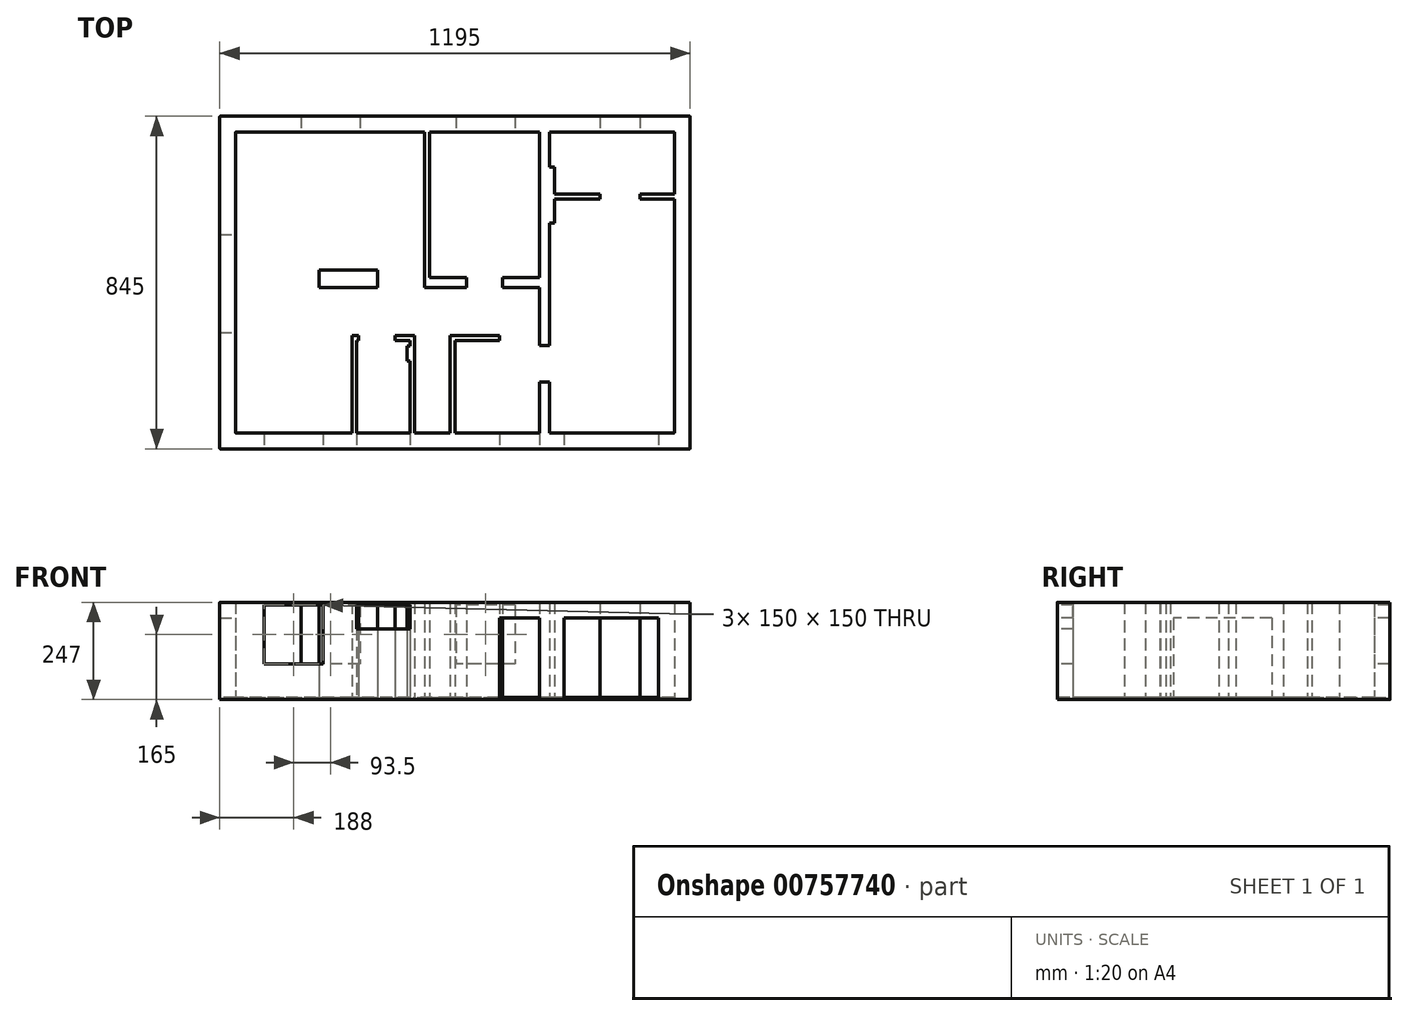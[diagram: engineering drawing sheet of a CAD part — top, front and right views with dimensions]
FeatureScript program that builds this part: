
annotation { "Feature Type Name" : "Feature", "Feature Type Description" : "" }
export const myFeature = defineFeature(function(context is Context, id is Id, definition is map)
    precondition{}
    {
        {
            var Q0;
            Q0=qCreatedBy(makeId("Top.planeOp"),FACE);
            var sketch = newSketch(context, id + "F0", { "sketchPlane" : qUnion([Q0])});
            skLineSegment(sketch, "E0", {"start": v(0, 0) * mm, "end": v(1145, 0) * mm, "construction": true});
            skLineSegment(sketch, "E1", {"start": v(1145, 0) * mm, "end": v(1145, 795) * mm, "construction": true});
            skLineSegment(sketch, "E2", {"start": v(1145, 795) * mm, "end": v(0, 795) * mm, "construction": true});
            skLineSegment(sketch, "E3", {"start": v(0, 795) * mm, "end": v(0, 0) * mm, "construction": true});
            skLineSegment(sketch, "E4", {"start": v(800, 0) * mm, "end": v(800, 795) * mm, "construction": true});
            skLineSegment(sketch, "E5", {"start": v(800, 397.5) * mm, "end": v(0, 397.5) * mm, "construction": true});
            skLineSegment(sketch, "E6.0", {"start": v(1170, 820) * mm, "end": v(-25, 820) * mm});
            skLineSegment(sketch, "E6.1", {"start": v(1170, -25) * mm, "end": v(1170, 820) * mm});
            skLineSegment(sketch, "E6.2", {"start": v(-25, -25) * mm, "end": v(1170, -25) * mm});
            skLineSegment(sketch, "E6.3", {"start": v(-25, 820) * mm, "end": v(-25, -25) * mm});
            skLineSegment(sketch, "E7.0", {"start": v(1130, 780) * mm, "end": v(15, 780) * mm});
            skLineSegment(sketch, "E7.1", {"start": v(1130, 15) * mm, "end": v(1130, 780) * mm});
            skLineSegment(sketch, "E7.2", {"start": v(15, 15) * mm, "end": v(1130, 15) * mm});
            skLineSegment(sketch, "E7.3", {"start": v(15, 780) * mm, "end": v(15, 15) * mm});
            skLineSegment(sketch, "E8.0", {"start": v(812.5, 0) * mm, "end": v(812.5, 795) * mm});
            skLineSegment(sketch, "E9.0", {"start": v(800, 410) * mm, "end": v(0, 410) * mm});
            skLineSegment(sketch, "E10.0", {"start": v(800, 385) * mm, "end": v(0, 385) * mm});
            skLineSegment(sketch, "E11.0", {"start": v(787.5, 0) * mm, "end": v(787.5, 795) * mm});
            skLineSegment(sketch, "E12", {"start": v(1090, 15) * mm, "end": v(1090, -25) * mm});
            skLineSegment(sketch, "E13", {"start": v(850, 15) * mm, "end": v(850, -25) * mm});
            skLineSegment(sketch, "E14", {"start": v(787.5, 15) * mm, "end": v(787.5, -25) * mm});
            skLineSegment(sketch, "E15", {"start": v(685.5, 15) * mm, "end": v(685.5, -25) * mm});
            skLineSegment(sketch, "E16", {"start": v(572.5, 15) * mm, "end": v(572.5, 250.5) * mm});
            skLineSegment(sketch, "E17", {"start": v(572.5, 250.5) * mm, "end": v(685.5, 250.5) * mm});
            skLineSegment(sketch, "E18.0", {"start": v(560.5, 262.5) * mm, "end": v(685.5, 262.5) * mm});
            skLineSegment(sketch, "E18.1", {"start": v(560.5, 15) * mm, "end": v(560.5, 262.5) * mm});
            skLineSegment(sketch, "E19", {"start": v(685.5, 262.5) * mm, "end": v(685.5, 250.5) * mm});
            skLineSegment(sketch, "E20", {"start": v(470.5, 15) * mm, "end": v(470.5, 262.5) * mm});
            skLineSegment(sketch, "E21", {"start": v(470.5, 262.5) * mm, "end": v(420, 262.5) * mm});
            skLineSegment(sketch, "E22", {"start": v(420, 262.5) * mm, "end": v(420, 250.5) * mm});
            skLineSegment(sketch, "E23", {"start": v(420, 250.5) * mm, "end": v(458.5, 250.5) * mm});
            skLineSegment(sketch, "E24", {"start": v(458.5, 250.5) * mm, "end": v(458.5, 236.22) * mm});
            skLineSegment(sketch, "E25", {"start": v(458.5, 236.22) * mm, "end": v(450.5, 236.22) * mm});
            skLineSegment(sketch, "E26", {"start": v(450.5, 236.22) * mm, "end": v(450.5, 198.5) * mm});
            skLineSegment(sketch, "E27", {"start": v(450.5, 198.5) * mm, "end": v(458.5, 198.5) * mm});
            skLineSegment(sketch, "E28", {"start": v(458.5, 198.5) * mm, "end": v(458.5, 15) * mm});
            skLineSegment(sketch, "E29", {"start": v(787.5, 145) * mm, "end": v(812.5, 145) * mm});
            skLineSegment(sketch, "E30", {"start": v(787.5, 237) * mm, "end": v(812.5, 237) * mm});
            skLineSegment(sketch, "E31", {"start": v(693.5, 410) * mm, "end": v(693.5, 385) * mm});
            skLineSegment(sketch, "E32", {"start": v(601.5, 410) * mm, "end": v(601.5, 385) * mm});
            skLineSegment(sketch, "E33", {"start": v(507.5, 780) * mm, "end": v(507.5, 410) * mm});
            skLineSegment(sketch, "E34", {"start": v(495.5, 780) * mm, "end": v(495.5, 410) * mm});
            skLineSegment(sketch, "E35", {"start": v(495.5, 410) * mm, "end": v(495.5, 385) * mm});
            skLineSegment(sketch, "E36", {"start": v(812.5, 691) * mm, "end": v(825.5, 691) * mm});
            skLineSegment(sketch, "E37", {"start": v(825.5, 691) * mm, "end": v(825.5, 549) * mm});
            skLineSegment(sketch, "E38", {"start": v(825.5, 549) * mm, "end": v(812.5, 549) * mm});
            skLineSegment(sketch, "E39", {"start": v(825.5, 622) * mm, "end": v(1130, 622) * mm});
            skLineSegment(sketch, "E40", {"start": v(825.5, 610) * mm, "end": v(1130, 610) * mm});
            skLineSegment(sketch, "E41", {"start": v(940.5, 622) * mm, "end": v(940.5, 610) * mm});
            skLineSegment(sketch, "E42", {"start": v(1042.5, 622) * mm, "end": v(1042.5, 610) * mm});
            skLineSegment(sketch, "E43", {"start": v(940.5, 820) * mm, "end": v(940.5, 780) * mm});
            skLineSegment(sketch, "E44", {"start": v(1042.5, 820) * mm, "end": v(1042.5, 780) * mm});
            skLineSegment(sketch, "E45", {"start": v(375.5, 385) * mm, "end": v(375.5, 429) * mm});
            skLineSegment(sketch, "E46", {"start": v(375.5, 429) * mm, "end": v(227.5, 429) * mm});
            skLineSegment(sketch, "E47", {"start": v(227.5, 429) * mm, "end": v(227.5, 385) * mm});
            skLineSegment(sketch, "E48", {"start": v(-25, 520) * mm, "end": v(15, 520) * mm});
            skLineSegment(sketch, "E49", {"start": v(-25, 270) * mm, "end": v(15, 270) * mm});
            skLineSegment(sketch, "E50", {"start": v(311, 15) * mm, "end": v(311, 262.5) * mm});
            skLineSegment(sketch, "E51", {"start": v(311, 262.5) * mm, "end": v(328, 262.5) * mm});
            skLineSegment(sketch, "E52", {"start": v(328, 262.5) * mm, "end": v(328, 250.5) * mm});
            skLineSegment(sketch, "E53", {"start": v(328, 250.5) * mm, "end": v(323, 250.5) * mm});
            skLineSegment(sketch, "E54", {"start": v(323, 250.5) * mm, "end": v(323, 15) * mm});
            skLineSegment(sketch, "E55", {"start": v(181.5, 820) * mm, "end": v(181.5, 780) * mm});
            skLineSegment(sketch, "E56", {"start": v(331.5, 820) * mm, "end": v(331.5, 780) * mm});
            skLineSegment(sketch, "E57", {"start": v(575, 820) * mm, "end": v(575, 780) * mm});
            skLineSegment(sketch, "E58", {"start": v(725, 820) * mm, "end": v(725, 780) * mm});
            skLineSegment(sketch, "E59", {"start": v(88, 15) * mm, "end": v(88, -25) * mm});
            skLineSegment(sketch, "E60", {"start": v(238, 15) * mm, "end": v(238, -25) * mm});
            skLineSegment(sketch, "E61", {"start": v(323, 15) * mm, "end": v(323, -25) * mm});
            skLineSegment(sketch, "E62", {"start": v(458.5, 15) * mm, "end": v(458.5, -25) * mm});
            skSolve(sketch);
        }
        {
            var Q0;
            {var subQ5=sQuery(id+"F0.wireOp",EDGE,"E6.1");Q0=makeQuery(id+"F0.imprint","IMPRINT",FACE,{"disambiguationData":[TD([[makeQuery(id+"F0.imprint","IMPRINT",EDGE,{"derivedFrom":subQ5}),1.0]])]});}
            var Q1;
            {var subQ0=sQuery(id+"F0.wireOp",EDGE,"E43");Q1=makeQuery(id+"F0.imprint","IMPRINT",FACE,{"disambiguationData":[TD([[makeQuery(id+"F0.imprint","IMPRINT",EDGE,{"derivedFrom":subQ0}),1.0]])]});}
            var Q2;
            {var subQ4=sQuery(id+"F0.wireOp",EDGE,"E43");Q2=makeQuery(id+"F0.imprint","IMPRINT",FACE,{"disambiguationData":[TD([[makeQuery(id+"F0.imprint","IMPRINT",EDGE,{"derivedFrom":subQ4}),-1.0]])]});}
            var Q3;
            {var subQ5=sQuery(id+"F0.wireOp",EDGE,"E48");Q3=makeQuery(id+"F0.imprint","IMPRINT",FACE,{"disambiguationData":[TD([[makeQuery(id+"F0.imprint","IMPRINT",EDGE,{"derivedFrom":subQ5}),-1.0]])]});}
            var Q4;
            {var subQ3=sQuery(id+"F0.wireOp",EDGE,"E15");Q4=makeQuery(id+"F0.imprint","IMPRINT",FACE,{"disambiguationData":[TD([[makeQuery(id+"F0.imprint","IMPRINT",EDGE,{"derivedFrom":subQ3}),-1.0]])]});}
            var Q5;
            {var subQ0=sQuery(id+"F0.wireOp",EDGE,"E14");Q5=makeQuery(id+"F0.imprint","IMPRINT",FACE,{"disambiguationData":[TD([[makeQuery(id+"F0.imprint","IMPRINT",EDGE,{"derivedFrom":subQ0}),-1.0]])]});}
            var Q6;
            {var subQ4=sQuery(id+"F0.wireOp",EDGE,"E13");Q6=makeQuery(id+"F0.imprint","IMPRINT",FACE,{"disambiguationData":[TD([[makeQuery(id+"F0.imprint","IMPRINT",EDGE,{"derivedFrom":subQ4}),-1.0]])]});}
            var Q7;
            {var subQ2=sQuery(id+"F0.wireOp",EDGE,"E12");Q7=makeQuery(id+"F0.imprint","IMPRINT",FACE,{"disambiguationData":[TD([[makeQuery(id+"F0.imprint","IMPRINT",EDGE,{"derivedFrom":subQ2}),-1.0]])]});}
            var Q8;
            {var subQ0=sQuery(id+"F0.wireOp",EDGE,"E38");Q8=makeQuery(id+"F0.imprint","IMPRINT",FACE,{"disambiguationData":[TD([[makeQuery(id+"F0.imprint","IMPRINT",EDGE,{"derivedFrom":subQ0}),1.0]])]});}
            var Q9;
            {var subQ3=sQuery(id+"F0.wireOp",EDGE,"E31");Q9=makeQuery(id+"F0.imprint","IMPRINT",FACE,{"disambiguationData":[TD([[makeQuery(id+"F0.imprint","IMPRINT",EDGE,{"derivedFrom":subQ3}),1.0]])]});}
            var Q10;
            {var subQ0=sQuery(id+"F0.wireOp",EDGE,"E47");var subQ1=sQuery(id+"F0.wireOp",EDGE,"E9.0");var subQ2=makeQuery(id+"F0.imprint","INTERSECT",VERTEX,{"derivedFrom":[subQ1,subQ0]});Q10=makeQuery(id+"F0.imprint","IMPRINT",FACE,{"disambiguationData":[TD([[makeQuery(id+"F0.imprint","IMPRINT",EDGE,{"disambiguationData":[TD([[subQ2,1.0]])],"derivedFrom":subQ1}),1.0]])]});}
            var Q11;
            {var subQ0=sQuery(id+"F0.wireOp",EDGE,"E31");Q11=makeQuery(id+"F0.imprint","IMPRINT",FACE,{"disambiguationData":[TD([[makeQuery(id+"F0.imprint","IMPRINT",EDGE,{"derivedFrom":subQ0}),-1.0]])]});}
            var Q12;
            {var subQ0=sQuery(id+"F0.wireOp",EDGE,"E32");Q12=makeQuery(id+"F0.imprint","IMPRINT",FACE,{"disambiguationData":[TD([[makeQuery(id+"F0.imprint","IMPRINT",EDGE,{"derivedFrom":subQ0}),-1.0]])]});}
            var Q13;
            {var subQ0=sQuery(id+"F0.wireOp",EDGE,"E35");Q13=makeQuery(id+"F0.imprint","IMPRINT",FACE,{"disambiguationData":[TD([[makeQuery(id+"F0.imprint","IMPRINT",EDGE,{"derivedFrom":subQ0}),-1.0]])]});}
            var Q14;
            {var subQ1=sQuery(id+"F0.wireOp",EDGE,"E36");Q14=makeQuery(id+"F0.imprint","IMPRINT",FACE,{"disambiguationData":[TD([[makeQuery(id+"F0.imprint","IMPRINT",EDGE,{"derivedFrom":subQ1}),-1.0]])]});}
            var Q15;
            {var subQ5=sQuery(id+"F0.wireOp",EDGE,"E46");Q15=makeQuery(id+"F0.imprint","IMPRINT",FACE,{"disambiguationData":[TD([[makeQuery(id+"F0.imprint","IMPRINT",EDGE,{"derivedFrom":subQ5}),1.0]])]});}
            var Q16;
            {var subQ4=sQuery(id+"F0.wireOp",EDGE,"E34");Q16=makeQuery(id+"F0.imprint","IMPRINT",FACE,{"disambiguationData":[TD([[makeQuery(id+"F0.imprint","IMPRINT",EDGE,{"derivedFrom":subQ4}),-1.0]])]});}
            var Q17;
            {var subQ8=sQuery(id+"F0.wireOp",EDGE,"E36");Q17=makeQuery(id+"F0.imprint","IMPRINT",FACE,{"disambiguationData":[TD([[makeQuery(id+"F0.imprint","IMPRINT",EDGE,{"derivedFrom":subQ8}),1.0]])]});}
            var Q18;
            {var subQ0=sQuery(id+"F0.wireOp",EDGE,"E50");Q18=makeQuery(id+"F0.imprint","IMPRINT",FACE,{"disambiguationData":[TD([[makeQuery(id+"F0.imprint","IMPRINT",EDGE,{"derivedFrom":subQ0}),-1.0]])]});}
            var Q19;
            {var subQ13=sQuery(id+"F0.wireOp",EDGE,"E16");Q19=makeQuery(id+"F0.imprint","IMPRINT",FACE,{"disambiguationData":[TD([[makeQuery(id+"F0.imprint","IMPRINT",EDGE,{"derivedFrom":subQ13}),-1.0]])]});}
            var Q20;
            {var subQ4=sQuery(id+"F0.wireOp",EDGE,"E30");Q20=makeQuery(id+"F0.imprint","IMPRINT",FACE,{"disambiguationData":[TD([[makeQuery(id+"F0.imprint","IMPRINT",EDGE,{"derivedFrom":subQ4}),1.0]])]});}
            var Q21;
            {var subQ2=sQuery(id+"F0.wireOp",EDGE,"E29");Q21=makeQuery(id+"F0.imprint","IMPRINT",FACE,{"disambiguationData":[TD([[makeQuery(id+"F0.imprint","IMPRINT",EDGE,{"derivedFrom":subQ2}),1.0]])]});}
            var Q22;
            {var subQ0=sQuery(id+"F0.wireOp",EDGE,"E41");Q22=makeQuery(id+"F0.imprint","IMPRINT",FACE,{"disambiguationData":[TD([[makeQuery(id+"F0.imprint","IMPRINT",EDGE,{"derivedFrom":subQ0}),1.0]])]});}
            var Q23;
            {var subQ0=sQuery(id+"F0.wireOp",EDGE,"E16");Q23=makeQuery(id+"F0.imprint","IMPRINT",FACE,{"disambiguationData":[TD([[makeQuery(id+"F0.imprint","IMPRINT",EDGE,{"derivedFrom":subQ0}),1.0]])]});}
            var Q24;
            {var subQ2=sQuery(id+"F0.wireOp",EDGE,"E33");Q24=makeQuery(id+"F0.imprint","IMPRINT",FACE,{"disambiguationData":[TD([[makeQuery(id+"F0.imprint","IMPRINT",EDGE,{"derivedFrom":subQ2}),-1.0]])]});}
            var Q25;
            {var subQ5=sQuery(id+"F0.wireOp",EDGE,"E42");Q25=makeQuery(id+"F0.imprint","IMPRINT",FACE,{"disambiguationData":[TD([[makeQuery(id+"F0.imprint","IMPRINT",EDGE,{"derivedFrom":subQ5}),1.0]])]});}
            var Q26;
            {var subQ5=sQuery(id+"F0.wireOp",EDGE,"E29");Q26=makeQuery(id+"F0.imprint","IMPRINT",FACE,{"disambiguationData":[TD([[makeQuery(id+"F0.imprint","IMPRINT",EDGE,{"derivedFrom":subQ5}),-1.0]])]});}
            var Q27;
            {var subQ0=sQuery(id+"F0.wireOp",EDGE,"E10.0");var subQ1=sQuery(id+"F0.wireOp",EDGE,"E7.3");var subQ2=makeQuery(id+"F0.imprint","INTERSECT",VERTEX,{"derivedFrom":[subQ1,subQ0]});Q27=makeQuery(id+"F0.imprint","IMPRINT",FACE,{"disambiguationData":[TD([[makeQuery(id+"F0.imprint","IMPRINT",EDGE,{"disambiguationData":[TD([[subQ2,1.0]])],"derivedFrom":subQ1}),1.0]])]});}
            var Q28;
            {var subQ0=sQuery(id+"F0.wireOp",EDGE,"E20");Q28=makeQuery(id+"F0.imprint","IMPRINT",FACE,{"disambiguationData":[TD([[makeQuery(id+"F0.imprint","IMPRINT",EDGE,{"derivedFrom":subQ0}),1.0]])]});}
            var Q29;
            {var subQ5=sQuery(id+"F0.wireOp",EDGE,"E41");Q29=makeQuery(id+"F0.imprint","IMPRINT",FACE,{"disambiguationData":[TD([[makeQuery(id+"F0.imprint","IMPRINT",EDGE,{"derivedFrom":subQ5}),-1.0]])]});}
            var Q30;
            {var subQ2=sQuery(id+"F0.wireOp",EDGE,"E33");Q30=makeQuery(id+"F0.imprint","IMPRINT",FACE,{"disambiguationData":[TD([[makeQuery(id+"F0.imprint","IMPRINT",EDGE,{"derivedFrom":subQ2}),1.0]])]});}
            var Q31;
            {var subQ3=sQuery(id+"F0.wireOp",EDGE,"E48");Q31=makeQuery(id+"F0.imprint","IMPRINT",FACE,{"disambiguationData":[TD([[makeQuery(id+"F0.imprint","IMPRINT",EDGE,{"derivedFrom":subQ3}),1.0]])]});}
            var Q32;
            {var subQ0=sQuery(id+"F0.wireOp",EDGE,"E55");Q32=makeQuery(id+"F0.imprint","IMPRINT",FACE,{"disambiguationData":[TD([[makeQuery(id+"F0.imprint","IMPRINT",EDGE,{"derivedFrom":subQ0}),1.0]])]});}
            var Q33;
            {var subQ4=sQuery(id+"F0.wireOp",EDGE,"E56");Q33=makeQuery(id+"F0.imprint","IMPRINT",FACE,{"disambiguationData":[TD([[makeQuery(id+"F0.imprint","IMPRINT",EDGE,{"derivedFrom":subQ4}),1.0]])]});}
            var Q34;
            {var subQ0=sQuery(id+"F0.wireOp",EDGE,"E57");Q34=makeQuery(id+"F0.imprint","IMPRINT",FACE,{"disambiguationData":[TD([[makeQuery(id+"F0.imprint","IMPRINT",EDGE,{"derivedFrom":subQ0}),1.0]])]});}
            var Q35;
            {var subQ0=sQuery(id+"F0.wireOp",EDGE,"E49");Q35=makeQuery(id+"F0.imprint","IMPRINT",FACE,{"disambiguationData":[TD([[makeQuery(id+"F0.imprint","IMPRINT",EDGE,{"derivedFrom":subQ0}),-1.0]])]});}
            var Q36;
            {var subQ0=sQuery(id+"F0.wireOp",EDGE,"E59");Q36=makeQuery(id+"F0.imprint","IMPRINT",FACE,{"disambiguationData":[TD([[makeQuery(id+"F0.imprint","IMPRINT",EDGE,{"derivedFrom":subQ0}),1.0]])]});}
            var Q37;
            {var subQ3=sQuery(id+"F0.wireOp",EDGE,"E60");Q37=makeQuery(id+"F0.imprint","IMPRINT",FACE,{"disambiguationData":[TD([[makeQuery(id+"F0.imprint","IMPRINT",EDGE,{"derivedFrom":subQ3}),1.0]])]});}
            var Q38;
            {var subQ0=sQuery(id+"F0.wireOp",EDGE,"E61");Q38=makeQuery(id+"F0.imprint","IMPRINT",FACE,{"disambiguationData":[TD([[makeQuery(id+"F0.imprint","IMPRINT",EDGE,{"derivedFrom":subQ0}),1.0]])]});}
            extrude(context, id + "F1", {"entities" : qUnion([Q0, Q1, Q2, Q3, Q4, Q5, Q6, Q7, Q8, Q9, Q10, Q11, Q12, Q13, Q14, Q15, Q16, Q17, Q18, Q19, Q20, Q21, Q22, Q23, Q24, Q25, Q26, Q27, Q28, Q29, Q30, Q31, Q32, Q33, Q34, Q35, Q36, Q37, Q38]), "depth" : 5 * mm, "offsetDistance" : 25 * mm});
        }
        {
            var Q0;
            {var subQ5=sQuery(id+"F0.wireOp",EDGE,"E6.1");Q0=makeQuery(id+"F0.imprint","IMPRINT",FACE,{"disambiguationData":[TD([[makeQuery(id+"F0.imprint","IMPRINT",EDGE,{"derivedFrom":subQ5}),1.0]])]});}
            var Q1;
            {var subQ4=sQuery(id+"F0.wireOp",EDGE,"E43");Q1=makeQuery(id+"F0.imprint","IMPRINT",FACE,{"disambiguationData":[TD([[makeQuery(id+"F0.imprint","IMPRINT",EDGE,{"derivedFrom":subQ4}),-1.0]])]});}
            var Q2;
            {var subQ3=sQuery(id+"F0.wireOp",EDGE,"E15");Q2=makeQuery(id+"F0.imprint","IMPRINT",FACE,{"disambiguationData":[TD([[makeQuery(id+"F0.imprint","IMPRINT",EDGE,{"derivedFrom":subQ3}),-1.0]])]});}
            var Q3;
            {var subQ4=sQuery(id+"F0.wireOp",EDGE,"E13");Q3=makeQuery(id+"F0.imprint","IMPRINT",FACE,{"disambiguationData":[TD([[makeQuery(id+"F0.imprint","IMPRINT",EDGE,{"derivedFrom":subQ4}),-1.0]])]});}
            var Q4;
            {var subQ5=sQuery(id+"F0.wireOp",EDGE,"E29");Q4=makeQuery(id+"F0.imprint","IMPRINT",FACE,{"disambiguationData":[TD([[makeQuery(id+"F0.imprint","IMPRINT",EDGE,{"derivedFrom":subQ5}),-1.0]])]});}
            var Q5;
            {var subQ4=sQuery(id+"F0.wireOp",EDGE,"E30");Q5=makeQuery(id+"F0.imprint","IMPRINT",FACE,{"disambiguationData":[TD([[makeQuery(id+"F0.imprint","IMPRINT",EDGE,{"derivedFrom":subQ4}),1.0]])]});}
            var Q6;
            {var subQ1=sQuery(id+"F0.wireOp",EDGE,"E36");Q6=makeQuery(id+"F0.imprint","IMPRINT",FACE,{"disambiguationData":[TD([[makeQuery(id+"F0.imprint","IMPRINT",EDGE,{"derivedFrom":subQ1}),-1.0]])]});}
            var Q7;
            {var subQ5=sQuery(id+"F0.wireOp",EDGE,"E41");Q7=makeQuery(id+"F0.imprint","IMPRINT",FACE,{"disambiguationData":[TD([[makeQuery(id+"F0.imprint","IMPRINT",EDGE,{"derivedFrom":subQ5}),-1.0]])]});}
            var Q8;
            {var subQ5=sQuery(id+"F0.wireOp",EDGE,"E42");Q8=makeQuery(id+"F0.imprint","IMPRINT",FACE,{"disambiguationData":[TD([[makeQuery(id+"F0.imprint","IMPRINT",EDGE,{"derivedFrom":subQ5}),1.0]])]});}
            var Q9;
            {var subQ3=sQuery(id+"F0.wireOp",EDGE,"E31");Q9=makeQuery(id+"F0.imprint","IMPRINT",FACE,{"disambiguationData":[TD([[makeQuery(id+"F0.imprint","IMPRINT",EDGE,{"derivedFrom":subQ3}),1.0]])]});}
            var Q10;
            {var subQ0=sQuery(id+"F0.wireOp",EDGE,"E32");Q10=makeQuery(id+"F0.imprint","IMPRINT",FACE,{"disambiguationData":[TD([[makeQuery(id+"F0.imprint","IMPRINT",EDGE,{"derivedFrom":subQ0}),-1.0]])]});}
            var Q11;
            {var subQ2=sQuery(id+"F0.wireOp",EDGE,"E33");Q11=makeQuery(id+"F0.imprint","IMPRINT",FACE,{"disambiguationData":[TD([[makeQuery(id+"F0.imprint","IMPRINT",EDGE,{"derivedFrom":subQ2}),-1.0]])]});}
            var Q12;
            {var subQ5=sQuery(id+"F0.wireOp",EDGE,"E46");Q12=makeQuery(id+"F0.imprint","IMPRINT",FACE,{"disambiguationData":[TD([[makeQuery(id+"F0.imprint","IMPRINT",EDGE,{"derivedFrom":subQ5}),1.0]])]});}
            var Q13;
            {var subQ0=sQuery(id+"F0.wireOp",EDGE,"E47");var subQ1=sQuery(id+"F0.wireOp",EDGE,"E9.0");var subQ2=makeQuery(id+"F0.imprint","INTERSECT",VERTEX,{"derivedFrom":[subQ1,subQ0]});Q13=makeQuery(id+"F0.imprint","IMPRINT",FACE,{"disambiguationData":[TD([[makeQuery(id+"F0.imprint","IMPRINT",EDGE,{"disambiguationData":[TD([[subQ2,1.0]])],"derivedFrom":subQ1}),1.0]])]});}
            var Q14;
            {var subQ0=sQuery(id+"F0.wireOp",EDGE,"E50");Q14=makeQuery(id+"F0.imprint","IMPRINT",FACE,{"disambiguationData":[TD([[makeQuery(id+"F0.imprint","IMPRINT",EDGE,{"derivedFrom":subQ0}),-1.0]])]});}
            var Q15;
            {var subQ0=sQuery(id+"F0.wireOp",EDGE,"E20");Q15=makeQuery(id+"F0.imprint","IMPRINT",FACE,{"disambiguationData":[TD([[makeQuery(id+"F0.imprint","IMPRINT",EDGE,{"derivedFrom":subQ0}),1.0]])]});}
            var Q16;
            {var subQ0=sQuery(id+"F0.wireOp",EDGE,"E16");Q16=makeQuery(id+"F0.imprint","IMPRINT",FACE,{"disambiguationData":[TD([[makeQuery(id+"F0.imprint","IMPRINT",EDGE,{"derivedFrom":subQ0}),1.0]])]});}
            var Q17;
            {var subQ0=sQuery(id+"F0.wireOp",EDGE,"E49");Q17=makeQuery(id+"F0.imprint","IMPRINT",FACE,{"disambiguationData":[TD([[makeQuery(id+"F0.imprint","IMPRINT",EDGE,{"derivedFrom":subQ0}),-1.0]])]});}
            var Q18;
            {var subQ3=sQuery(id+"F0.wireOp",EDGE,"E60");Q18=makeQuery(id+"F0.imprint","IMPRINT",FACE,{"disambiguationData":[TD([[makeQuery(id+"F0.imprint","IMPRINT",EDGE,{"derivedFrom":subQ3}),1.0]])]});}
            var Q19;
            {var subQ0=sQuery(id+"F0.wireOp",EDGE,"E61");Q19=makeQuery(id+"F0.imprint","IMPRINT",FACE,{"disambiguationData":[TD([[makeQuery(id+"F0.imprint","IMPRINT",EDGE,{"derivedFrom":subQ0}),1.0]])]});}
            var Q20;
            {var subQ0=sQuery(id+"F0.wireOp",EDGE,"E59");Q20=makeQuery(id+"F0.imprint","IMPRINT",FACE,{"disambiguationData":[TD([[makeQuery(id+"F0.imprint","IMPRINT",EDGE,{"derivedFrom":subQ0}),1.0]])]});}
            var Q21;
            {var subQ3=sQuery(id+"F0.wireOp",EDGE,"E48");Q21=makeQuery(id+"F0.imprint","IMPRINT",FACE,{"disambiguationData":[TD([[makeQuery(id+"F0.imprint","IMPRINT",EDGE,{"derivedFrom":subQ3}),1.0]])]});}
            var Q22;
            {var subQ0=sQuery(id+"F0.wireOp",EDGE,"E55");Q22=makeQuery(id+"F0.imprint","IMPRINT",FACE,{"disambiguationData":[TD([[makeQuery(id+"F0.imprint","IMPRINT",EDGE,{"derivedFrom":subQ0}),1.0]])]});}
            var Q23;
            {var subQ4=sQuery(id+"F0.wireOp",EDGE,"E56");Q23=makeQuery(id+"F0.imprint","IMPRINT",FACE,{"disambiguationData":[TD([[makeQuery(id+"F0.imprint","IMPRINT",EDGE,{"derivedFrom":subQ4}),1.0]])]});}
            var Q24;
            {var subQ0=sQuery(id+"F0.wireOp",EDGE,"E57");Q24=makeQuery(id+"F0.imprint","IMPRINT",FACE,{"disambiguationData":[TD([[makeQuery(id+"F0.imprint","IMPRINT",EDGE,{"derivedFrom":subQ0}),1.0]])]});}
            extrude(context, id + "F2", {"entities" : qUnion([Q0, Q1, Q2, Q3, Q4, Q5, Q6, Q7, Q8, Q9, Q10, Q11, Q12, Q13, Q14, Q15, Q16, Q17, Q18, Q19, Q20, Q21, Q22, Q23, Q24]), "operationType" : NewBodyOperationType.ADD, "depth" : 247 * mm, "offsetDistance" : 25 * mm});
        }
        {
            var Q0;
            Q0=makeQuery(id+"F2.opExtrude","CAP_FACE",FACE,{"disambiguationData":[OSD([sQuery(id+"F0.wireOp",EDGE,"E6.0"),sQuery(id+"F0.wireOp",EDGE,"E6.3"),sQuery(id+"F0.wireOp",EDGE,"E7.0"),sQuery(id+"F0.wireOp",EDGE,"E7.3"),sQuery(id+"F0.wireOp",EDGE,"E8.0"),sQuery(id+"F0.wireOp",EDGE,"E9.0"),sQuery(id+"F0.wireOp",EDGE,"E10.0"),sQuery(id+"F0.wireOp",EDGE,"E11.0"),sQuery(id+"F0.wireOp",EDGE,"E30"),sQuery(id+"F0.wireOp",EDGE,"E31"),sQuery(id+"F0.wireOp",EDGE,"E32"),sQuery(id+"F0.wireOp",EDGE,"E33"),sQuery(id+"F0.wireOp",EDGE,"E34"),sQuery(id+"F0.wireOp",EDGE,"E35"),sQuery(id+"F0.wireOp",EDGE,"E36"),sQuery(id+"F0.wireOp",EDGE,"E37"),sQuery(id+"F0.wireOp",EDGE,"E38"),sQuery(id+"F0.wireOp",EDGE,"E39"),sQuery(id+"F0.wireOp",EDGE,"E40"),sQuery(id+"F0.wireOp",EDGE,"E41"),sQuery(id+"F0.wireOp",EDGE,"E43"),sQuery(id+"F0.wireOp",EDGE,"E48")])],"isStart":false});
            var sketch = newSketch(context, id + "F3", { "sketchPlane" : qUnion([Q0])});
            skLineSegment(sketch, "E63.0", {"start": v(15, 780) * mm, "end": v(15, 15) * mm});
            skLineSegment(sketch, "E64.0", {"start": v(-25, 820) * mm, "end": v(-25, -25) * mm});
            skLineSegment(sketch, "E65.0", {"start": v(-25, 520) * mm, "end": v(15, 520) * mm});
            skLineSegment(sketch, "E66.0", {"start": v(-25, 270) * mm, "end": v(15, 270) * mm});
            skLineSegment(sketch, "E67.0", {"start": v(1170, 820) * mm, "end": v(-25, 820) * mm});
            skLineSegment(sketch, "E68.0", {"start": v(1130, 780) * mm, "end": v(15, 780) * mm});
            skLineSegment(sketch, "E69.0", {"start": v(940.5, 820) * mm, "end": v(940.5, 780) * mm});
            skLineSegment(sketch, "E70.0", {"start": v(1042.5, 820) * mm, "end": v(1042.5, 780) * mm});
            skLineSegment(sketch, "E71.0", {"start": v(-25, -25) * mm, "end": v(1170, -25) * mm});
            skLineSegment(sketch, "E72.0", {"start": v(15, 15) * mm, "end": v(1130, 15) * mm});
            skLineSegment(sketch, "E73.0", {"start": v(850, 15) * mm, "end": v(850, -25) * mm});
            skLineSegment(sketch, "E74.0", {"start": v(1090, 15) * mm, "end": v(1090, -25) * mm});
            skLineSegment(sketch, "E75.0", {"start": v(685.5, 15) * mm, "end": v(685.5, -25) * mm});
            skLineSegment(sketch, "E76.0", {"start": v(787.5, 15) * mm, "end": v(787.5, -25) * mm});
            skSolve(sketch);
        }
        {
            var Q0;
            {var subQ0=sQuery(id+"F3.wireOp",EDGE,"E65.0");Q0=makeQuery(id+"F3.imprint","IMPRINT",FACE,{"disambiguationData":[TD([[makeQuery(id+"F3.imprint","IMPRINT",EDGE,{"derivedFrom":subQ0}),-1.0]])]});}
            var Q1;
            {var subQ0=sQuery(id+"F3.wireOp",EDGE,"E75.0");Q1=makeQuery(id+"F3.imprint","IMPRINT",FACE,{"disambiguationData":[TD([[makeQuery(id+"F3.imprint","IMPRINT",EDGE,{"derivedFrom":subQ0}),1.0]])]});}
            var Q2;
            {var subQ0=sQuery(id+"F3.wireOp",EDGE,"E73.0");Q2=makeQuery(id+"F3.imprint","IMPRINT",FACE,{"disambiguationData":[TD([[makeQuery(id+"F3.imprint","IMPRINT",EDGE,{"derivedFrom":subQ0}),1.0]])]});}
            var Q3;
            {var subQ0=sQuery(id+"F3.wireOp",EDGE,"E69.0");Q3=makeQuery(id+"F3.imprint","IMPRINT",FACE,{"disambiguationData":[TD([[makeQuery(id+"F3.imprint","IMPRINT",EDGE,{"derivedFrom":subQ0}),1.0]])]});}
            extrude(context, id + "F4", {"entities" : qUnion([Q0, Q1, Q2, Q3]), "operationType" : NewBodyOperationType.ADD, "oppositeDirection" : true, "depth" : (247 - 207) * mm, "offsetDistance" : 25 * mm});
        }
        {
            var Q0;
            Q0=qCreatedBy(makeId("Top.planeOp"),FACE);
            cPlane(context, id + "F5", {"entities" : qUnion([Q0]), "cplaneType" : CPlaneType.OFFSET, "offset" : 90 * mm, "width" : 150 * mm, "height" : 150 * mm});
        }
        {
            var Q0;
            Q0=qCreatedBy(id+"F5.planeOp",FACE);
            var sketch = newSketch(context, id + "F6", { "sketchPlane" : qUnion([Q0])});
            skLineSegment(sketch, "E77.0", {"start": v(1170, 820) * mm, "end": v(575, 820) * mm});
            skLineSegment(sketch, "E78.0", {"start": v(1130, 780) * mm, "end": v(575, 780) * mm});
            skLineSegment(sketch, "E79.0", {"start": v(331.5, 820) * mm, "end": v(331.5, 780) * mm});
            skLineSegment(sketch, "E80.0", {"start": v(181.5, 820) * mm, "end": v(181.5, 780) * mm});
            skLineSegment(sketch, "E81.0", {"start": v(575, 820) * mm, "end": v(575, 780) * mm});
            skLineSegment(sketch, "E82.0", {"start": v(725, 820) * mm, "end": v(725, 780) * mm});
            skLineSegment(sketch, "E83.0", {"start": v(15, 15) * mm, "end": v(238, 15) * mm});
            skLineSegment(sketch, "E84.0", {"start": v(-25, -25) * mm, "end": v(238, -25) * mm});
            skLineSegment(sketch, "E85.0", {"start": v(88, 15) * mm, "end": v(88, -25) * mm});
            skLineSegment(sketch, "E86.0", {"start": v(238, 15) * mm, "end": v(238, -25) * mm});
            skLineSegment(sketch, "E87.trimOffspring", {"start": v(331.5, 780) * mm, "end": v(15, 780) * mm});
            skLineSegment(sketch, "E88.trimOffspring", {"start": v(331.5, 820) * mm, "end": v(-25, 820) * mm});
            skPoint(sketch, "E89.0.end.orphan", {"position": v(323, -25) * mm});
            skPoint(sketch, "E89.0.start.orphan", {"position": v(323, 15) * mm});
            skPoint(sketch, "E90.trimOffspring.end.orphan", {"position": v(1170, -25) * mm});
            skPoint(sketch, "E90.trimOffspring.start.orphan", {"position": v(458.5, -25) * mm});
            skPoint(sketch, "E91.trimOffspring.end.orphan", {"position": v(1130, 15) * mm});
            skPoint(sketch, "E91.trimOffspring.start.orphan", {"position": v(458.5, 15) * mm});
            skSolve(sketch);
        }
        {
            var Q0;
            Q0 = qSketchRegion(id + "F6", true);
            extrude(context, id + "F7", {"entities" : qUnion([Q0]), "operationType" : NewBodyOperationType.REMOVE, "depth" : (240 - 90) * mm, "offsetDistance" : 25 * mm});
        }
        {
            var Q0;
            Q0=makeQuery(id+"F7.boolean.opBoolean","COPY",FACE,{"derivedFrom":makeQuery(id+"F7.opExtrude","CAP_FACE",FACE,{"disambiguationData":[OSD([sQuery(id+"F6.wireOp",EDGE,"E83.0"),sQuery(id+"F6.wireOp",EDGE,"E84.0"),sQuery(id+"F6.wireOp",EDGE,"E85.0"),sQuery(id+"F6.wireOp",EDGE,"E86.0")])],"isStart":false})});
            var sketch = newSketch(context, id + "F8", { "sketchPlane" : qUnion([Q0])});
            skLineSegment(sketch, "E92.0", {"start": v(323, -15) * mm, "end": v(323, 25) * mm});
            skLineSegment(sketch, "E93.0", {"start": v(15, -15) * mm, "end": v(1130, -15) * mm});
            skLineSegment(sketch, "E94.0", {"start": v(-25, 25) * mm, "end": v(1170, 25) * mm});
            skLineSegment(sketch, "E95.0", {"start": v(458.5, -15) * mm, "end": v(458.5, 25) * mm});
            skSolve(sketch);
        }
        {
            var Q0;
            Q0 = qSketchRegion(id + "F8", true);
            extrude(context, id + "F9", {"entities" : qUnion([Q0]), "operationType" : NewBodyOperationType.REMOVE, "depth" : 60 * mm, "offsetDistance" : 25 * mm});
        }
        {
            var Q0;
            {var subQ0=sQuery(id+"F0.wireOp",EDGE,"E6.3");var subQ1=sQuery(id+"F0.wireOp",EDGE,"E6.2");Q0=makeQuery(id+"F2.boolean.opBoolean","MERGE",EDGE,{"derivedFrom":[makeQuery(id+"F1.opExtrude","SWEPT_EDGE",EDGE,{"disambiguationData":[OSD([subQ1,subQ0])]}),makeQuery(id+"F2.opExtrude","SWEPT_EDGE",EDGE,{"disambiguationData":[OSD([subQ1,subQ0])]})]});}
            var Q1;
            {var subQ0=sQuery(id+"F0.wireOp",EDGE,"E6.2");var subQ1=sQuery(id+"F0.wireOp",EDGE,"E6.1");Q1=makeQuery(id+"F2.boolean.opBoolean","MERGE",EDGE,{"derivedFrom":[makeQuery(id+"F1.opExtrude","SWEPT_EDGE",EDGE,{"disambiguationData":[OSD([subQ1,subQ0])]}),makeQuery(id+"F2.opExtrude","SWEPT_EDGE",EDGE,{"disambiguationData":[OSD([subQ1,subQ0])]})]});}
            var Q2;
            {var subQ0=sQuery(id+"F0.wireOp",EDGE,"E6.1");var subQ1=sQuery(id+"F0.wireOp",EDGE,"E6.0");Q2=makeQuery(id+"F2.boolean.opBoolean","MERGE",EDGE,{"derivedFrom":[makeQuery(id+"F1.opExtrude","SWEPT_EDGE",EDGE,{"disambiguationData":[OSD([subQ1,subQ0])]}),makeQuery(id+"F2.opExtrude","SWEPT_EDGE",EDGE,{"disambiguationData":[OSD([subQ1,subQ0])]})]});}
            var Q3;
            {var subQ0=sQuery(id+"F0.wireOp",EDGE,"E6.3");var subQ1=sQuery(id+"F0.wireOp",EDGE,"E6.0");Q3=makeQuery(id+"F2.boolean.opBoolean","MERGE",EDGE,{"derivedFrom":[makeQuery(id+"F1.opExtrude","SWEPT_EDGE",EDGE,{"disambiguationData":[OSD([subQ1,subQ0])]}),makeQuery(id+"F2.opExtrude","SWEPT_EDGE",EDGE,{"disambiguationData":[OSD([subQ1,subQ0])]})]});}
            var Q4;
            Q4=makeQuery(id+"F2.opExtrude","SWEPT_EDGE",EDGE,{"disambiguationData":[OSD([sQuery(id+"F0.wireOp",EDGE,"E7.1"),sQuery(id+"F0.wireOp",EDGE,"E7.2")])]});
            var Q5;
            Q5=makeQuery(id+"F2.opExtrude","SWEPT_EDGE",EDGE,{"disambiguationData":[OSD([sQuery(id+"F0.wireOp",EDGE,"E7.2"),sQuery(id+"F0.wireOp",EDGE,"E7.3")])]});
            var Q6;
            Q6=makeQuery(id+"F2.opExtrude","SWEPT_EDGE",EDGE,{"disambiguationData":[OSD([sQuery(id+"F0.wireOp",EDGE,"E7.0"),sQuery(id+"F0.wireOp",EDGE,"E7.3")])]});
            var Q7;
            Q7=makeQuery(id+"F2.opExtrude","SWEPT_EDGE",EDGE,{"disambiguationData":[OSD([sQuery(id+"F0.wireOp",EDGE,"E7.0"),sQuery(id+"F0.wireOp",EDGE,"E7.1")])]});
            fillet(context, id + "F10", {"entities" : qUnion([Q0, Q1, Q2, Q3, Q4, Q5, Q6, Q7]), "radius" : 1 * mm, "tangentPropagation" : true, "allowEdgeOverflow" : false});
        }
    });
